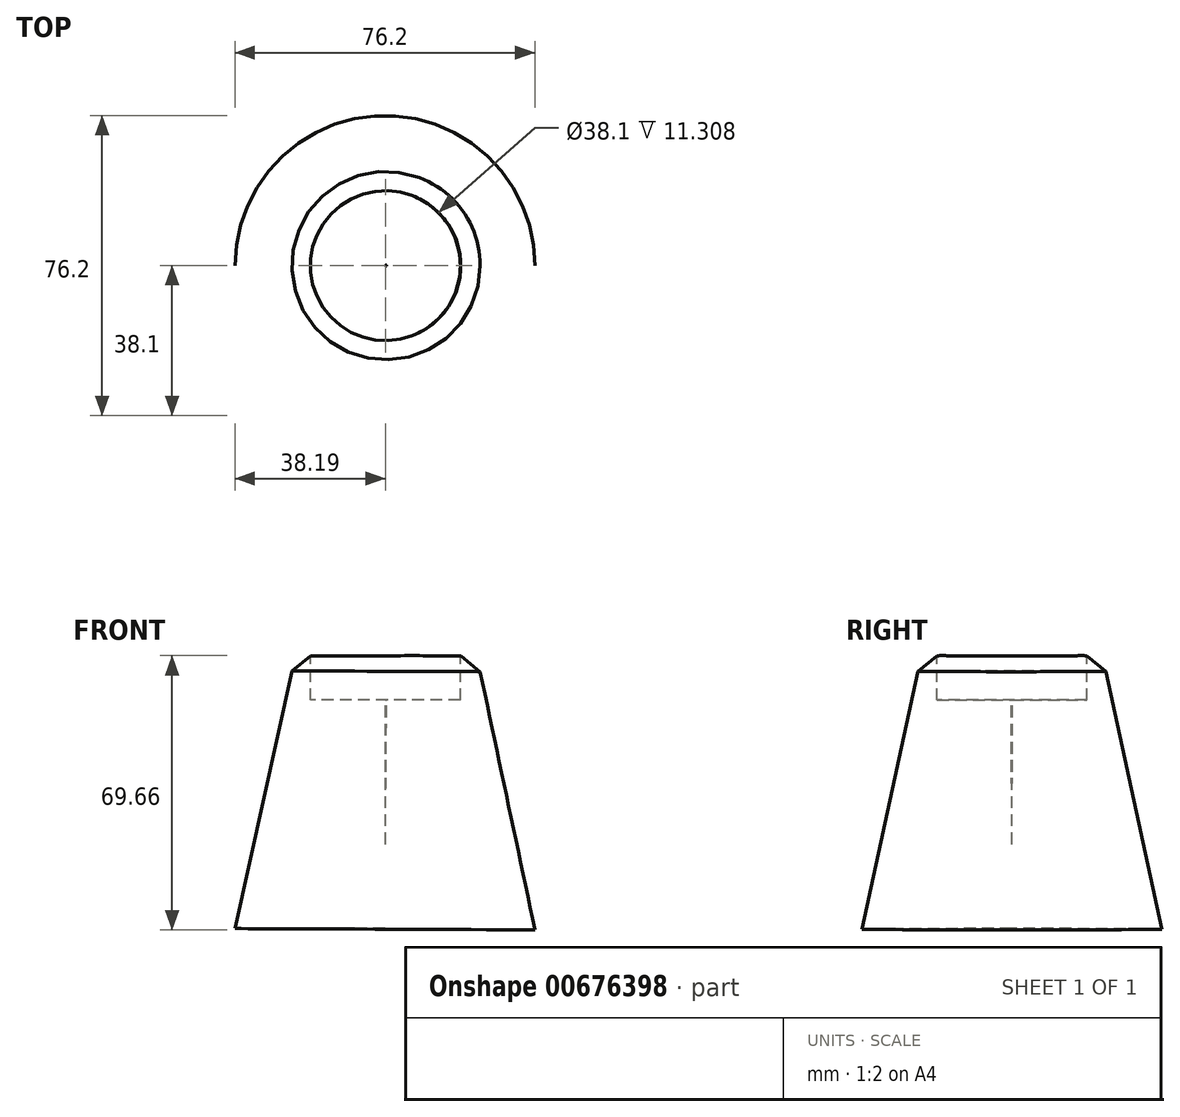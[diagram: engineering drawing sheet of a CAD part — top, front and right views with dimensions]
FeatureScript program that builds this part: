
annotation { "Feature Type Name" : "Feature", "Feature Type Description" : "" }
export const myFeature = defineFeature(function(context is Context, id is Id, definition is map)
    precondition{}
    {
        {
            var Q0;
            Q0=qCreatedBy(makeId("Front.planeOp"),FACE);
            var sketch = newSketch(context, id + "F0", { "sketchPlane" : qUnion([Q0])});
            skLineSegment(sketch, "E0", {"start": v(0, 30.06) * mm, "end": v(-22.86, 30.06) * mm});
            skLineSegment(sketch, "E1", {"start": v(-22.86, 30.06) * mm, "end": v(-38.19, -39.39) * mm});
            skLineSegment(sketch, "E2", {"start": v(-38.19, -39.39) * mm, "end": v(-0.09, -39.39) * mm});
            skLineSegment(sketch, "E3", {"start": v(0, 30.06) * mm, "end": v(0, -17.95) * mm});
            skLineSegment(sketch, "E4", {"start": v(0, -17.95) * mm, "end": v(-0.09, -39.39) * mm});
            skLineSegment(sketch, "E5", {"start": v(0, -17.95) * mm, "end": v(0, -17.95) * mm});
            skSolve(sketch);
        }
        {
            var Q0;
            Q0=makeQuery(id+"F0.imprint","IMPRINT",FACE,{"disambiguationData":[TD([[makeQuery(id+"F0.imprint","IMPRINT",EDGE,{"derivedFrom":sQuery(id+"F0.wireOp",EDGE,"E0")}),1.0]])]});
            var Q1;
            Q1=sQuery(id+"F0.wireOp",EDGE,"E4");
            revolve(context, id + "F1", {"entities" : qUnion([Q0]), "axis" : qUnion([Q1]), "revolveType" : RevolveType.FULL});
        }
        {
            var Q0;
            Q0=makeQuery(id+"F1.opRevolve","SWEPT_EDGE",EDGE,{"disambiguationData":[OSD([sQuery(id+"F0.wireOp",EDGE,"E0"),sQuery(id+"F0.wireOp",EDGE,"E1")])]});
            chamfer(context, id + "F2", {"entities" : qUnion([Q0]), "width" : 5.08 * mm, "tangentPropagation" : true});
        }
        {
            var Q0;
            Q0=qCreatedBy(makeId("Top.planeOp"),FACE);
            cPlane(context, id + "F3", {"entities" : qUnion([Q0]), "cplaneType" : CPlaneType.OFFSET, "offset" : 30.07 * mm, "width" : 152.4 * mm, "height" : 152.4 * mm});
        }
        {
            var Q0;
            Q0=qCreatedBy(id+"F3.planeOp",FACE);
            var sketch = newSketch(context, id + "F4", { "sketchPlane" : qUnion([Q0])});
            skCircle(sketch, "E6", {"center": v(0, 0) * mm, "radius": 19.05 * mm});
            skSolve(sketch);
        }
        {
            var Q0;
            Q0 = qSketchRegion(id + "F4", true);
            extrude(context, id + "F5", {"entities" : qUnion([Q0]), "operationType" : NewBodyOperationType.REMOVE, "oppositeDirection" : true, "depth" : 11.43 * mm, "offsetDistance" : 25.4 * mm});
        }
    });
